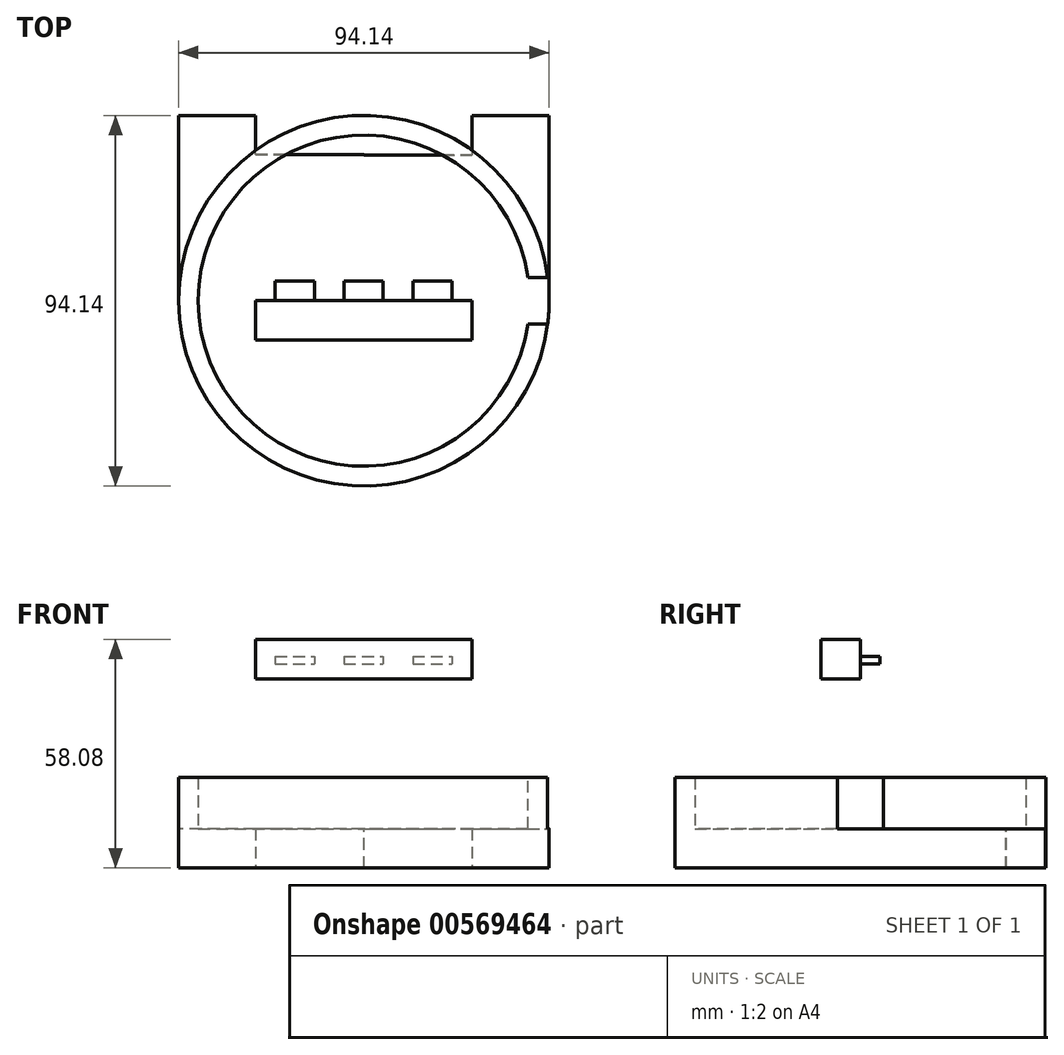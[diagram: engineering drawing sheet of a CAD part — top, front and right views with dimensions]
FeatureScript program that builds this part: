
annotation { "Feature Type Name" : "Feature", "Feature Type Description" : "" }
export const myFeature = defineFeature(function(context is Context, id is Id, definition is map)
    precondition{}
    {
        {
            var Q0;
            Q0=qCreatedBy(makeId("Front.planeOp"),FACE);
            var sketch = newSketch(context, id + "F0", { "sketchPlane" : qUnion([Q0])});
            skLineSegment(sketch, "E0.bottom", {"start": v(-27.57, 38.08) * mm, "end": v(27.43, 38.08) * mm});
            skLineSegment(sketch, "E0.top", {"start": v(-27.57, 48.08) * mm, "end": v(27.43, 48.08) * mm});
            skLineSegment(sketch, "E0.left", {"start": v(-27.57, 38.08) * mm, "end": v(-27.57, 48.08) * mm});
            skLineSegment(sketch, "E0.right", {"start": v(27.43, 38.08) * mm, "end": v(27.43, 48.08) * mm});
            skLineSegment(sketch, "E1.bottom", {"start": v(-22.57, 43.83) * mm, "end": v(-12.57, 43.83) * mm});
            skLineSegment(sketch, "E1.top", {"start": v(-22.57, 41.83) * mm, "end": v(-12.57, 41.83) * mm});
            skLineSegment(sketch, "E1.left", {"start": v(-22.57, 43.83) * mm, "end": v(-22.57, 41.83) * mm});
            skLineSegment(sketch, "E1.right", {"start": v(-12.57, 43.83) * mm, "end": v(-12.57, 41.83) * mm});
            skLineSegment(sketch, "E2.bottom", {"start": v(-5.07, 43.83) * mm, "end": v(4.93, 43.83) * mm});
            skLineSegment(sketch, "E2.top", {"start": v(-5.07, 41.83) * mm, "end": v(4.93, 41.83) * mm});
            skLineSegment(sketch, "E2.left", {"start": v(-5.07, 43.83) * mm, "end": v(-5.07, 41.83) * mm});
            skLineSegment(sketch, "E2.right", {"start": v(4.93, 43.83) * mm, "end": v(4.93, 41.83) * mm});
            skLineSegment(sketch, "E3.bottom", {"start": v(12.43, 43.83) * mm, "end": v(22.43, 43.83) * mm});
            skLineSegment(sketch, "E3.top", {"start": v(12.43, 41.83) * mm, "end": v(22.43, 41.83) * mm});
            skLineSegment(sketch, "E3.left", {"start": v(12.43, 43.83) * mm, "end": v(12.43, 41.83) * mm});
            skLineSegment(sketch, "E3.right", {"start": v(22.43, 43.83) * mm, "end": v(22.43, 41.83) * mm});
            skSolve(sketch);
        }
        {
            var Q0;
            Q0 = qSketchRegion(id + "F0", true);
            var Q1;
            Q1=makeQuery(id+"F0.imprint","IMPRINT",FACE,{"disambiguationData":[TD([[makeQuery(id+"F0.imprint","IMPRINT",EDGE,{"derivedFrom":sQuery(id+"F0.wireOp",EDGE,"E1.bottom")}),-1.0]])]});
            var Q2;
            Q2=makeQuery(id+"F0.imprint","IMPRINT",FACE,{"disambiguationData":[TD([[makeQuery(id+"F0.imprint","IMPRINT",EDGE,{"derivedFrom":sQuery(id+"F0.wireOp",EDGE,"E2.bottom")}),-1.0]])]});
            var Q3;
            Q3=makeQuery(id+"F0.imprint","IMPRINT",FACE,{"disambiguationData":[TD([[makeQuery(id+"F0.imprint","IMPRINT",EDGE,{"derivedFrom":sQuery(id+"F0.wireOp",EDGE,"E3.bottom")}),-1.0]])]});
            extrude(context, id + "F1", {"entities" : qUnion([Q0, Q1, Q2, Q3]), "depth" : 10 * mm, "offsetDistance" : 25 * mm});
        }
        {
            var Q0;
            Q0=qCreatedBy(makeId("Front.planeOp"),FACE);
            var sketch = newSketch(context, id + "F2", { "sketchPlane" : qUnion([Q0])});
            skLineSegment(sketch, "E4", {"start": v(-42.08, 13) * mm, "end": v(-42.08, 0) * mm});
            skLineSegment(sketch, "E5", {"start": v(0, 0) * mm, "end": v(-42.08, 0) * mm});
            skLineSegment(sketch, "E6", {"start": v(-42.08, 13) * mm, "end": v(-47.07, 13) * mm});
            skLineSegment(sketch, "E7", {"start": v(-47.07, 13) * mm, "end": v(-47.07, -10) * mm});
            skLineSegment(sketch, "E8", {"start": v(-47.07, -10) * mm, "end": v(0, -10) * mm});
            skLineSegment(sketch, "E9", {"start": v(0, -10) * mm, "end": v(0, 0) * mm});
            skLineSegment(sketch, "E10", {"start": v(-42.08, 0) * mm, "end": v(-47.07, 0) * mm});
            skSolve(sketch);
        }
        {
            var Q0;
            Q0=makeQuery(id+"F0.imprint","IMPRINT",FACE,{"disambiguationData":[TD([[makeQuery(id+"F0.imprint","IMPRINT",EDGE,{"derivedFrom":sQuery(id+"F0.wireOp",EDGE,"E3.bottom")}),-1.0]])]});
            var Q1;
            Q1=makeQuery(id+"F0.imprint","IMPRINT",FACE,{"disambiguationData":[TD([[makeQuery(id+"F0.imprint","IMPRINT",EDGE,{"derivedFrom":sQuery(id+"F0.wireOp",EDGE,"E2.bottom")}),-1.0]])]});
            var Q2;
            Q2=makeQuery(id+"F0.imprint","IMPRINT",FACE,{"disambiguationData":[TD([[makeQuery(id+"F0.imprint","IMPRINT",EDGE,{"derivedFrom":sQuery(id+"F0.wireOp",EDGE,"E1.bottom")}),-1.0]])]});
            extrude(context, id + "F3", {"entities" : qUnion([Q0, Q1, Q2]), "operationType" : NewBodyOperationType.ADD, "oppositeDirection" : true, "depth" : 5 * mm, "offsetDistance" : 25 * mm});
        }
        {
            var Q0;
            {var subQ2=sQuery(id+"F2.wireOp",EDGE,"E4");Q0=makeQuery(id+"F2.imprint","IMPRINT",FACE,{"disambiguationData":[TD([[makeQuery(id+"F2.imprint","IMPRINT",EDGE,{"derivedFrom":subQ2}),-1.0]])]});}
            var Q1;
            {var subQ0=sQuery(id+"F2.wireOp",EDGE,"E9");Q1=makeQuery(id+"F2.imprint","IMPRINT",FACE,{"disambiguationData":[TD([[makeQuery(id+"F2.imprint","IMPRINT",EDGE,{"derivedFrom":subQ0}),1.0]])]});}
            var Q2;
            Q2=sQuery(id+"F2.wireOp",EDGE,"E9");
            revolve(context, id + "F4", {"entities" : qUnion([Q0, Q1]), "axis" : qUnion([Q2]), "revolveType" : RevolveType.ONE_DIRECTION, "angle" : 180 * degree});
        }
        {
            var Q0;
            Q0=makeQuery(id+"F2.imprint","IMPRINT",FACE,{"disambiguationData":[TD([[makeQuery(id+"F2.imprint","IMPRINT",EDGE,{"derivedFrom":sQuery(id+"F2.wireOp",EDGE,"E5")}),1.0]])]});
            extrude(context, id + "F5", {"entities" : qUnion([Q0]), "operationType" : NewBodyOperationType.ADD, "oppositeDirection" : true, "depth" : 47.08 * mm, "offsetDistance" : 25 * mm});
        }
        {
            var Q0;
            Q0=makeQuery(id+"F2.imprint","IMPRINT",FACE,{"disambiguationData":[TD([[makeQuery(id+"F2.imprint","IMPRINT",EDGE,{"derivedFrom":sQuery(id+"F2.wireOp",EDGE,"E4")}),-1.0]])]});
            var Q1;
            Q1=sQuery(id+"F2.wireOp",EDGE,"E9");
            revolve(context, id + "F6", {"operationType" : NewBodyOperationType.ADD, "entities" : qUnion([Q0]), "axis" : qUnion([Q1]), "revolveType" : RevolveType.ONE_DIRECTION, "oppositeDirection" : true, "angle" : 90 * degree});
        }
        {
            var Q0;
            Q0=makeQuery(id+"F5.opExtrude","CAP_FACE",FACE,{"disambiguationData":[OSD([sQuery(id+"F2.wireOp",EDGE,"E5"),sQuery(id+"F2.wireOp",EDGE,"E7"),sQuery(id+"F2.wireOp",EDGE,"E8"),sQuery(id+"F2.wireOp",EDGE,"E9"),sQuery(id+"F2.wireOp",EDGE,"E10")])],"isStart":false});
            var sketch = newSketch(context, id + "F7", { "sketchPlane" : qUnion([Q0])});
            skLineSegment(sketch, "E11", {"start": v(27.5, 0) * mm, "end": v(27.5, -10) * mm});
            skSolve(sketch);
        }
        {
            var Q0;
            {var subQ0=sQuery(id+"F7.wireOp",EDGE,"E11");Q0=makeQuery(id+"F7.imprint","IMPRINT",FACE,{"disambiguationData":[TD([[makeQuery(id+"F7.imprint","IMPRINT",EDGE,{"derivedFrom":subQ0}),-1.0]])]});}
            extrude(context, id + "F8", {"entities" : qUnion([Q0]), "operationType" : NewBodyOperationType.REMOVE, "oppositeDirection" : true, "depth" : 10 * mm, "offsetDistance" : 25 * mm});
        }
        {
            var Q0;
            {var subQ0=sQuery(id+"F2.wireOp",EDGE,"E7");var subQ1=sQuery(id+"F2.wireOp",EDGE,"E6");var subQ2=sQuery(id+"F2.wireOp",EDGE,"E5");var subQ3=sQuery(id+"F2.wireOp",EDGE,"E4");var subQ4=sQuery(id+"F2.wireOp",EDGE,"E8");var subQ5=sQuery(id+"F2.wireOp",EDGE,"E9");Q0=makeQuery(id+"F5.boolean.opBoolean","SPLIT",FACE,{"disambiguationData":[TD([makeQuery(id+"F4.opRevolve","SWEPT_FACE",FACE,{"disambiguationData":[OSD([subQ4])]})])],"derivedFrom":makeQuery(id+"F4.opRevolve","CAP_FACE",FACE,{"disambiguationData":[OSD([subQ3,subQ2,subQ1,subQ0,subQ4,subQ5])],"isStart":false})});}
            var sketch = newSketch(context, id + "F9", { "sketchPlane" : qUnion([Q0])});
            skLineSegment(sketch, "E12", {"start": v(-42.08, 0) * mm, "end": v(-47.07, 0) * mm});
            skLineSegment(sketch, "E13", {"start": v(-27.5, 0) * mm, "end": v(-27.5, -10) * mm});
            skPoint(sketch, "E13.endSnap0", {"position": v(-23.54, -10) * mm});
            skSolve(sketch);
        }
        {
            var Q0;
            {var subQ0=sQuery(id+"F9.wireOp",EDGE,"E12");Q0=makeQuery(id+"F9.imprint","IMPRINT",FACE,{"disambiguationData":[TD([[makeQuery(id+"F9.imprint","IMPRINT",EDGE,{"derivedFrom":subQ0}),1.0]])]});}
            extrude(context, id + "F10", {"entities" : qUnion([Q0]), "operationType" : NewBodyOperationType.ADD, "depth" : 47.02 * mm, "offsetDistance" : 25 * mm});
        }
        {
            var Q0;
            {var subQ1=sQuery(id+"F2.wireOp",EDGE,"E5");var subQ3=sQuery(id+"F2.wireOp",EDGE,"E8");var subQ5=makeQuery(id+"F4.opRevolve","SWEPT_FACE",FACE,{"disambiguationData":[OSD([subQ3])]});var subQ7=sQuery(id+"F2.wireOp",EDGE,"E9");var subQ9=sQuery(id+"F2.wireOp",EDGE,"E7");var subQ10=sQuery(id+"F2.wireOp",EDGE,"E6");var subQ11=sQuery(id+"F2.wireOp",EDGE,"E4");Q0=makeQuery(id+"F10.boolean.opBoolean","SPLIT",FACE,{"disambiguationData":[TD([subQ5])],"derivedFrom":makeQuery(id+"F5.boolean.opBoolean","SPLIT",FACE,{"disambiguationData":[TD([subQ5])],"derivedFrom":makeQuery(id+"F4.opRevolve","CAP_FACE",FACE,{"disambiguationData":[OSD([subQ11,subQ1,subQ10,subQ9,subQ3,subQ7])],"isStart":false})})});}
            extrude(context, id + "F11", {"entities" : qUnion([Q0]), "operationType" : NewBodyOperationType.ADD, "depth" : 37.02 * mm, "offsetDistance" : 25 * mm});
        }
        {
            var Q0;
            {var subQ0=sQuery(id+"F2.wireOp",EDGE,"E7");var subQ2=sQuery(id+"F2.wireOp",EDGE,"E6");var subQ4=sQuery(id+"F2.wireOp",EDGE,"E5");var subQ6=sQuery(id+"F2.wireOp",EDGE,"E4");var subQ7=makeQuery(id+"F4.opRevolve","SWEPT_FACE",FACE,{"disambiguationData":[OSD([subQ6])]});var subQ9=sQuery(id+"F2.wireOp",EDGE,"E8");var subQ10=sQuery(id+"F2.wireOp",EDGE,"E9");Q0=makeQuery(id+"F10.boolean.opBoolean","SPLIT",FACE,{"disambiguationData":[TD([subQ7])],"derivedFrom":makeQuery(id+"F5.boolean.opBoolean","SPLIT",FACE,{"disambiguationData":[TD([makeQuery(id+"F4.opRevolve","SWEPT_FACE",FACE,{"disambiguationData":[OSD([subQ9])]})])],"derivedFrom":makeQuery(id+"F4.opRevolve","CAP_FACE",FACE,{"disambiguationData":[OSD([subQ6,subQ4,subQ2,subQ0,subQ9,subQ10])],"isStart":false})})});}
            var Q1;
            Q1=sQuery(id+"F2.wireOp",EDGE,"E9");
            revolve(context, id + "F12", {"operationType" : NewBodyOperationType.ADD, "entities" : qUnion([Q0]), "axis" : qUnion([Q1]), "revolveType" : RevolveType.ONE_DIRECTION, "angle" : 90 * degree});
        }
        {
            var Q0;
            {var subQ0=sQuery(id+"F2.wireOp",EDGE,"E6");Q0=makeQuery(id+"F12.boolean.opBoolean","MERGE",FACE,{"derivedFrom":[makeQuery(id+"F6.boolean.opBoolean","MERGE",FACE,{"derivedFrom":[makeQuery(id+"F4.opRevolve","SWEPT_FACE",FACE,{"disambiguationData":[OSD([subQ0])]}),makeQuery(id+"F6.opRevolve","SWEPT_FACE",FACE,{"disambiguationData":[OSD([subQ0])]})]}),makeQuery(id+"F12.opRevolve","SWEPT_FACE",FACE,{"disambiguationData":[OSD([subQ0])]})]});}
            var sketch = newSketch(context, id + "F13", { "sketchPlane" : qUnion([Q0])});
            skLineSegment(sketch, "E14", {"start": v(41.66, 5.88) * mm, "end": v(46.7, 5.88) * mm});
            skLineSegment(sketch, "E15", {"start": v(41.66, -5.88) * mm, "end": v(46.7, -5.88) * mm});
            skSolve(sketch);
        }
        {
            var Q0;
            {var subQ0=sQuery(id+"F13.wireOp",EDGE,"E14");Q0=makeQuery(id+"F13.imprint","IMPRINT",FACE,{"disambiguationData":[TD([[makeQuery(id+"F13.imprint","IMPRINT",EDGE,{"derivedFrom":subQ0}),-1.0]])]});}
            extrude(context, id + "F14", {"entities" : qUnion([Q0]), "operationType" : NewBodyOperationType.REMOVE, "oppositeDirection" : true, "depth" : 13 * mm, "offsetDistance" : 25 * mm});
        }
    });
